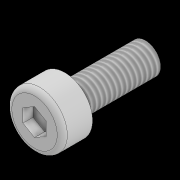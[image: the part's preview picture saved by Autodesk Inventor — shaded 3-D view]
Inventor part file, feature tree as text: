
AUTODESK INVENTOR PART (.ipt)
format: ipt  version: 2022.2 (Build 262287010, 287A)  size: 121,856 bytes
history: native  units: mm
features: extrude x3, sketch x1, fillet x1, thread x1
ambient origin geometry x8: Origin, YZ Plane, XZ Plane, XY Plane, X Axis, Y Axis, Z Axis, Center Point
bodies: Body1 (feature_tree)
feature tree (6):
  sketch  "Sketch3"  dims[d8=1.5mm d9=2.75mm d10=2.3mm d11=3.0mm d12=0.0mm d13=8.0mm d14=0.0mm d15=1.0mm d16=0.0mm d17=0.5mm d18=8.0mm d19=0.0mm]
  extrude  "Extrusion1"  Depth=2.75mm
  extrude  "Extrusion2"  Depth=2.3mm
  extrude  "Extrusion3"  Depth=3.0mm
  fillet  "Fillet1"  [1 undecoded]
  thread  "Thread2"  [1 undecoded]
note: 2 required parameter values undecoded (feature->parameter linkage not recoverable at this tier; creation-order binding heuristic only, values carry confidence <= 0.55)
